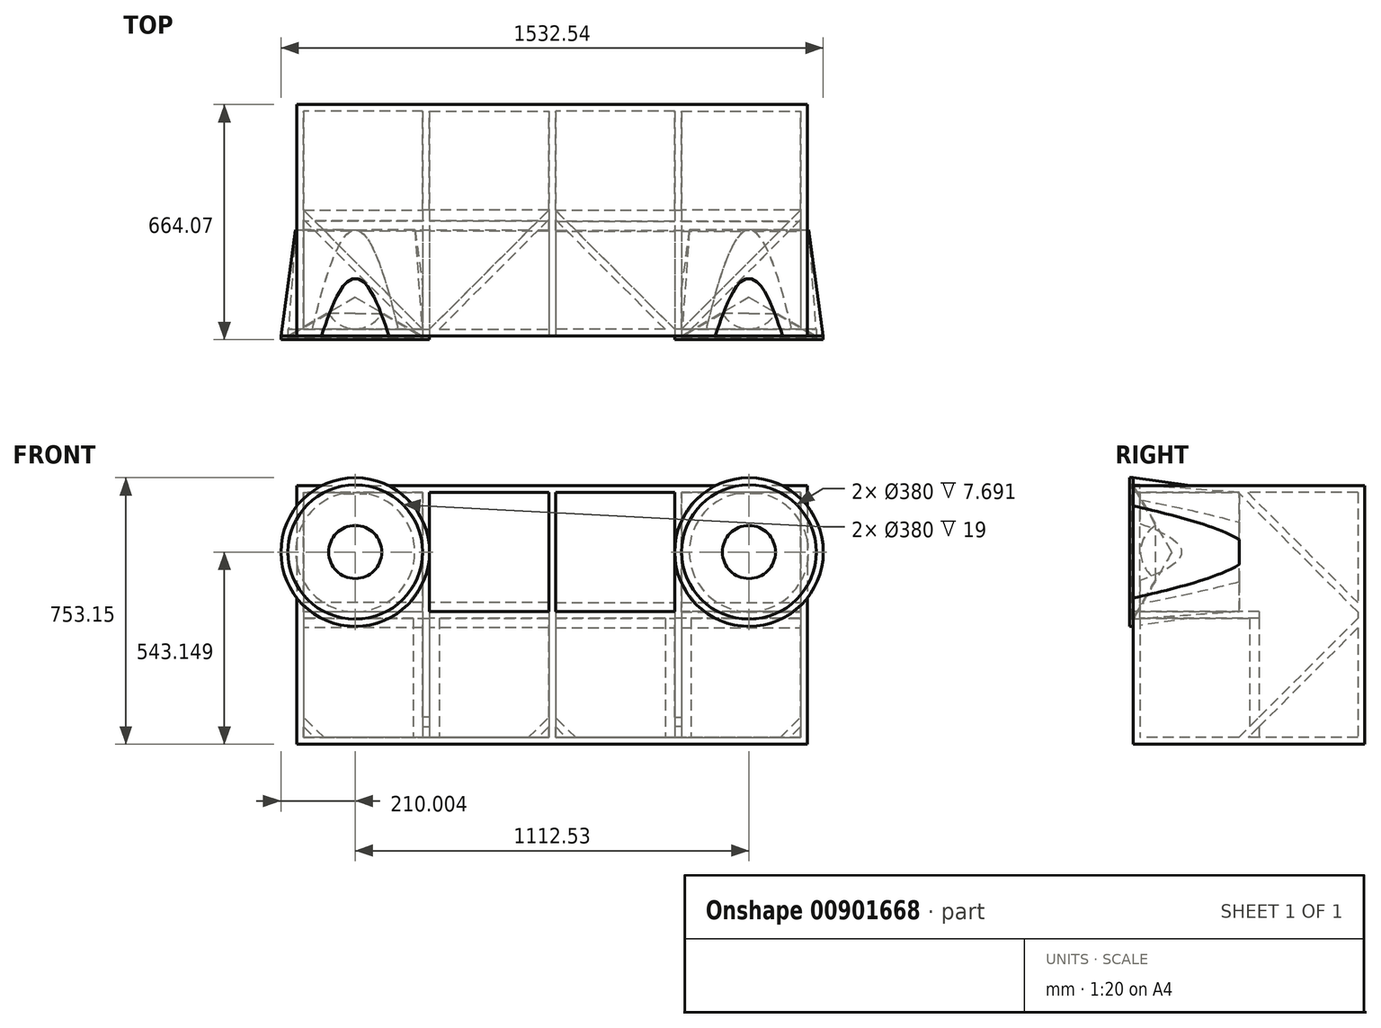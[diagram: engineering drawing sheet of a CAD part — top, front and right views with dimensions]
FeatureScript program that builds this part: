
annotation { "Feature Type Name" : "Feature", "Feature Type Description" : "" }
export const myFeature = defineFeature(function(context is Context, id is Id, definition is map)
    precondition{}
    {
        {
            assignVariable(context, id + "F0", {"variableType" : VariableType.LENGTH, "name" : "Dia", "lengthValue" : 380 * mm});
        }
        {
            assignVariable(context, id + "F1", {"variableType" : VariableType.LENGTH, "name" : "Side", "lengthValue" : sqrt(getVariable(context, 'Dia') * getVariable(context, 'Dia') * PI / 4)});
        }
        {
            assignVariable(context, id + "F2", {"variableType" : VariableType.LENGTH, "name" : "OutsideDia", "lengthValue" : getVariable(context, 'Dia') + 2 * 20 * mm});
        }
        {
            var Q0;
            Q0=qCreatedBy(makeId("Top.planeOp"),FACE);
            var sketch = newSketch(context, id + "F3", { "sketchPlane" : qUnion([Q0])});
            skLineSegment(sketch, "E0.bottom", {"start": v(-721.03, 654.07) * mm, "end": v(9.5, 654.07) * mm});
            skLineSegment(sketch, "E0.top", {"start": v(-721.03, 0) * mm, "end": v(9.5, 0) * mm});
            skLineSegment(sketch, "E0.left", {"start": v(-721.03, 654.07) * mm, "end": v(-721.03, 0) * mm});
            skLineSegment(sketch, "E0.right", {"start": v(9.5, 654.07) * mm, "end": v(9.5, 0) * mm});
            skLineSegment(sketch, "E1.bottom", {"start": v(-702.03, 635.07) * mm, "end": v(-365.27, 635.07) * mm});
            skLineSegment(sketch, "E1.top", {"start": v(-702.03, 19) * mm, "end": v(-392.14, 19) * mm});
            skLineSegment(sketch, "E1.left", {"start": v(-702.03, 635.07) * mm, "end": v(-702.03, 355.77) * mm});
            skLineSegment(sketch, "E1.right", {"start": v(-9.5, 635.07) * mm, "end": v(-9.5, 355.77) * mm});
            skLineSegment(sketch, "E2.top", {"start": v(-365.27, 355.77) * mm, "end": v(-346.27, 355.77) * mm});
            skLineSegment(sketch, "E2.left", {"start": v(-365.27, 635.07) * mm, "end": v(-365.27, 355.77) * mm});
            skLineSegment(sketch, "E2.right", {"start": v(-346.27, 635.07) * mm, "end": v(-346.27, 355.77) * mm});
            skLineSegment(sketch, "E3", {"start": v(-9.5, 355.77) * mm, "end": v(-346.27, 19) * mm});
            skLineSegment(sketch, "E4", {"start": v(-319.4, 19) * mm, "end": v(-9.5, 328.9) * mm});
            skLineSegment(sketch, "E5", {"start": v(-702.03, 355.77) * mm, "end": v(-365.27, 19) * mm});
            skLineSegment(sketch, "E6", {"start": v(-392.14, 19) * mm, "end": v(-702.03, 328.9) * mm});
            skLineSegment(sketch, "E7.trimOffspring", {"start": v(-346.27, 635.07) * mm, "end": v(-9.5, 635.07) * mm});
            skLineSegment(sketch, "E8.trimOffspring", {"start": v(-702.03, 328.9) * mm, "end": v(-702.03, 19) * mm});
            skLineSegment(sketch, "E9.trimOffspring", {"start": v(-365.27, 19) * mm, "end": v(-346.27, 19) * mm});
            skLineSegment(sketch, "E10.trimOffspring", {"start": v(-319.4, 19) * mm, "end": v(-9.5, 19) * mm});
            skLineSegment(sketch, "E11.trimOffspring", {"start": v(-9.5, 328.9) * mm, "end": v(-9.5, 19) * mm});
            skSolve(sketch);
        }
        {
            var Q0;
            Q0 = qSketchRegion(id + "F3", true);
            extrude(context, id + "F4", {"entities" : qUnion([Q0]), "depth" : getVariable(context, 'Side'), "offsetDistance" : 25 * mm});
        }
        {
            var Q0;
            Q0=makeQuery(id+"F4.opExtrude","SWEPT_FACE",FACE,{"disambiguationData":[OSD([sQuery(id+"F3.wireOp",EDGE,"E0.left")])]});
            var sketch = newSketch(context, id + "F5", { "sketchPlane" : qUnion([Q0])});
            skLineSegment(sketch, "E12", {"start": v(-635.07, 336.77) * mm, "end": v(-298.3, 0) * mm});
            skLineSegment(sketch, "E13", {"start": v(-298.3, 0) * mm, "end": v(-325.18, 0) * mm});
            skLineSegment(sketch, "E14", {"start": v(-325.18, 0) * mm, "end": v(-635.07, 309.9) * mm});
            skLineSegment(sketch, "E15", {"start": v(-635.07, 309.9) * mm, "end": v(-635.07, 336.77) * mm});
            skSolve(sketch);
        }
        {
            var Q0;
            Q0 = qSketchRegion(id + "F5", true);
            var Q1;
            Q1=makeQuery(id+"F4.opExtrude","SWEPT_FACE",FACE,{"disambiguationData":[OSD([sQuery(id+"F3.wireOp",EDGE,"E0.right")])]});
            extrude(context, id + "F6", {"entities" : qUnion([Q0]), "operationType" : NewBodyOperationType.ADD, "endBound" : BoundingType.UP_TO_SURFACE, "oppositeDirection" : true, "depth" : 25 * mm, "endBoundEntityFace" : qUnion([Q1]), "offsetDistance" : 25 * mm});
        }
        {
            var Q0;
            Q0=makeQuery(id+"F4.opExtrude","CAP_FACE",FACE,{"disambiguationData":[OSD([sQuery(id+"F3.wireOp",EDGE,"E0.bottom"),sQuery(id+"F3.wireOp",EDGE,"E0.top"),sQuery(id+"F3.wireOp",EDGE,"E0.left"),sQuery(id+"F3.wireOp",EDGE,"E0.right"),sQuery(id+"F3.wireOp",EDGE,"E1.bottom"),sQuery(id+"F3.wireOp",EDGE,"E1.top"),sQuery(id+"F3.wireOp",EDGE,"E1.left"),sQuery(id+"F3.wireOp",EDGE,"E1.right"),sQuery(id+"F3.wireOp",EDGE,"E2.top"),sQuery(id+"F3.wireOp",EDGE,"E2.left"),sQuery(id+"F3.wireOp",EDGE,"E2.right"),sQuery(id+"F3.wireOp",EDGE,"E3"),sQuery(id+"F3.wireOp",EDGE,"E4"),sQuery(id+"F3.wireOp",EDGE,"E5"),sQuery(id+"F3.wireOp",EDGE,"E6"),sQuery(id+"F3.wireOp",EDGE,"E7.trimOffspring"),sQuery(id+"F3.wireOp",EDGE,"E8.trimOffspring"),sQuery(id+"F3.wireOp",EDGE,"E9.trimOffspring"),sQuery(id+"F3.wireOp",EDGE,"E10.trimOffspring"),sQuery(id+"F3.wireOp",EDGE,"E11.trimOffspring")])],"isStart":false});
            var sketch = newSketch(context, id + "F7", { "sketchPlane" : qUnion([Q0])});
            skLineSegment(sketch, "E16.bottom", {"start": v(-721.03, 654.07) * mm, "end": v(9.5, 654.07) * mm});
            skLineSegment(sketch, "E16.top", {"start": v(-721.03, 0) * mm, "end": v(9.5, 0) * mm});
            skLineSegment(sketch, "E16.left", {"start": v(-721.03, 654.07) * mm, "end": v(-721.03, 0) * mm});
            skLineSegment(sketch, "E16.right", {"start": v(9.5, 654.07) * mm, "end": v(9.5, 0) * mm});
            skLineSegment(sketch, "E17.bottom", {"start": v(-702.03, 635.07) * mm, "end": v(-365.27, 635.07) * mm});
            skLineSegment(sketch, "E17.top", {"start": v(-702.03, 355.77) * mm, "end": v(-365.27, 355.77) * mm});
            skLineSegment(sketch, "E17.left", {"start": v(-702.03, 635.07) * mm, "end": v(-702.03, 355.77) * mm});
            skLineSegment(sketch, "E17.right", {"start": v(-365.27, 635.07) * mm, "end": v(-365.27, 355.77) * mm});
            skLineSegment(sketch, "E18.bottom", {"start": v(-9.5, 635.07) * mm, "end": v(-346.27, 635.07) * mm});
            skLineSegment(sketch, "E18.top", {"start": v(-9.5, 355.77) * mm, "end": v(-346.27, 355.77) * mm});
            skLineSegment(sketch, "E18.left", {"start": v(-9.5, 635.07) * mm, "end": v(-9.5, 355.77) * mm});
            skLineSegment(sketch, "E18.right", {"start": v(-346.27, 635.07) * mm, "end": v(-346.27, 355.77) * mm});
            skSolve(sketch);
        }
        {
            var Q0;
            Q0 = qSketchRegion(id + "F7", true);
            extrude(context, id + "F8", {"entities" : qUnion([Q0]), "operationType" : NewBodyOperationType.ADD, "depth" : 19 * mm, "offsetDistance" : 25 * mm});
        }
        {
            var Q0;
            Q0=makeQuery(id+"F8.opExtrude","CAP_FACE",FACE,{"disambiguationData":[OSD([sQuery(id+"F7.wireOp",EDGE,"E16.bottom"),sQuery(id+"F7.wireOp",EDGE,"E16.top"),sQuery(id+"F7.wireOp",EDGE,"E16.left"),sQuery(id+"F7.wireOp",EDGE,"E16.right"),sQuery(id+"F7.wireOp",EDGE,"E17.bottom"),sQuery(id+"F7.wireOp",EDGE,"E17.top"),sQuery(id+"F7.wireOp",EDGE,"E17.left"),sQuery(id+"F7.wireOp",EDGE,"E17.right"),sQuery(id+"F7.wireOp",EDGE,"E18.bottom"),sQuery(id+"F7.wireOp",EDGE,"E18.top"),sQuery(id+"F7.wireOp",EDGE,"E18.left"),sQuery(id+"F7.wireOp",EDGE,"E18.right")])],"isStart":false});
            var sketch = newSketch(context, id + "F9", { "sketchPlane" : qUnion([Q0])});
            skLineSegment(sketch, "E19.bottom", {"start": v(-721.03, 654.07) * mm, "end": v(9.5, 654.07) * mm});
            skLineSegment(sketch, "E19.top", {"start": v(-721.03, 0) * mm, "end": v(9.5, 0) * mm});
            skLineSegment(sketch, "E19.left", {"start": v(-721.03, 654.07) * mm, "end": v(-721.03, 0) * mm});
            skLineSegment(sketch, "E19.right", {"start": v(9.5, 654.07) * mm, "end": v(9.5, 0) * mm});
            skLineSegment(sketch, "E20.bottom", {"start": v(-702.03, 635.07) * mm, "end": v(-365.27, 635.07) * mm});
            skLineSegment(sketch, "E20.top", {"start": v(-702.03, 19) * mm, "end": v(-365.27, 19) * mm});
            skLineSegment(sketch, "E20.left", {"start": v(-702.03, 635.07) * mm, "end": v(-702.03, 19) * mm});
            skLineSegment(sketch, "E20.right", {"start": v(-365.27, 635.07) * mm, "end": v(-365.27, 19) * mm});
            skLineSegment(sketch, "E21.bottom", {"start": v(-9.5, 635.07) * mm, "end": v(-346.27, 635.07) * mm});
            skLineSegment(sketch, "E21.top", {"start": v(-9.5, 19) * mm, "end": v(-346.27, 19) * mm});
            skLineSegment(sketch, "E21.left", {"start": v(-9.5, 635.07) * mm, "end": v(-9.5, 19) * mm});
            skLineSegment(sketch, "E21.right", {"start": v(-346.27, 635.07) * mm, "end": v(-346.27, 19) * mm});
            skSolve(sketch);
        }
        {
            var Q0;
            Q0 = qSketchRegion(id + "F9", true);
            extrude(context, id + "F10", {"entities" : qUnion([Q0]), "operationType" : NewBodyOperationType.ADD, "depth" : getVariable(context, 'Side'), "offsetDistance" : 25 * mm});
        }
        {
            var Q0;
            Q0=makeQuery(id+"F10.boolean.opBoolean","MERGE",FACE,{"derivedFrom":[makeQuery(id+"F8.boolean.opBoolean","MERGE",FACE,{"derivedFrom":[makeQuery(id+"F4.opExtrude","SWEPT_FACE",FACE,{"disambiguationData":[OSD([sQuery(id+"F3.wireOp",EDGE,"E0.left")])]}),makeQuery(id+"F8.opExtrude","SWEPT_FACE",FACE,{"disambiguationData":[OSD([sQuery(id+"F7.wireOp",EDGE,"E16.left")])]})]}),makeQuery(id+"F10.opExtrude","SWEPT_FACE",FACE,{"disambiguationData":[OSD([sQuery(id+"F9.wireOp",EDGE,"E19.left")])]})]});
            var sketch = newSketch(context, id + "F11", { "sketchPlane" : qUnion([Q0])});
            skLineSegment(sketch, "E22", {"start": v(-323.62, 692.53) * mm, "end": v(-296.75, 692.53) * mm});
            skLineSegment(sketch, "E23", {"start": v(-296.75, 692.53) * mm, "end": v(-635.07, 354.21) * mm});
            skLineSegment(sketch, "E24", {"start": v(-635.07, 354.21) * mm, "end": v(-635.07, 381.08) * mm});
            skLineSegment(sketch, "E25", {"start": v(-635.07, 381.08) * mm, "end": v(-323.62, 692.53) * mm});
            skSolve(sketch);
        }
        {
            var Q0;
            Q0 = qSketchRegion(id + "F11", true);
            var Q1;
            Q1=makeQuery(id+"F10.boolean.opBoolean","MERGE",FACE,{"derivedFrom":[makeQuery(id+"F8.boolean.opBoolean","MERGE",FACE,{"derivedFrom":[makeQuery(id+"F4.opExtrude","SWEPT_FACE",FACE,{"disambiguationData":[OSD([sQuery(id+"F3.wireOp",EDGE,"E0.right")])]}),makeQuery(id+"F8.opExtrude","SWEPT_FACE",FACE,{"disambiguationData":[OSD([sQuery(id+"F7.wireOp",EDGE,"E16.right")])]})]}),makeQuery(id+"F10.opExtrude","SWEPT_FACE",FACE,{"disambiguationData":[OSD([sQuery(id+"F9.wireOp",EDGE,"E19.right")])]})]});
            extrude(context, id + "F12", {"entities" : qUnion([Q0]), "operationType" : NewBodyOperationType.ADD, "endBound" : BoundingType.UP_TO_SURFACE, "oppositeDirection" : true, "depth" : 25 * mm, "endBoundEntityFace" : qUnion([Q1]), "offsetDistance" : 25 * mm});
        }
        {
            var Q0;
            Q0=makeQuery(id+"F12.boolean.opBoolean","MERGE",FACE,{"derivedFrom":[makeQuery(id+"F10.opExtrude","CAP_FACE",FACE,{"disambiguationData":[OSD([sQuery(id+"F9.wireOp",EDGE,"E19.bottom"),sQuery(id+"F9.wireOp",EDGE,"E19.top"),sQuery(id+"F9.wireOp",EDGE,"E19.left"),sQuery(id+"F9.wireOp",EDGE,"E19.right"),sQuery(id+"F9.wireOp",EDGE,"E20.bottom"),sQuery(id+"F9.wireOp",EDGE,"E20.top"),sQuery(id+"F9.wireOp",EDGE,"E20.left"),sQuery(id+"F9.wireOp",EDGE,"E20.right"),sQuery(id+"F9.wireOp",EDGE,"E21.bottom"),sQuery(id+"F9.wireOp",EDGE,"E21.top"),sQuery(id+"F9.wireOp",EDGE,"E21.left"),sQuery(id+"F9.wireOp",EDGE,"E21.right")])],"isStart":false}),makeQuery(id+"F12.opExtrude","SWEPT_FACE",FACE,{"disambiguationData":[OSD([sQuery(id+"F11.wireOp",EDGE,"E22")])]})]});
            var sketch = newSketch(context, id + "F13", { "sketchPlane" : qUnion([Q0])});
            skLineSegment(sketch, "E26.bottom", {"start": v(-721.03, 654.07) * mm, "end": v(9.5, 654.07) * mm});
            skLineSegment(sketch, "E26.top", {"start": v(-721.03, 0) * mm, "end": v(9.5, 0) * mm});
            skLineSegment(sketch, "E26.left", {"start": v(-721.03, 654.07) * mm, "end": v(-721.03, 0) * mm});
            skLineSegment(sketch, "E26.right", {"start": v(9.5, 654.07) * mm, "end": v(9.5, 0) * mm});
            skSolve(sketch);
        }
        {
            var Q0;
            Q0 = qSketchRegion(id + "F13", true);
            extrude(context, id + "F14", {"entities" : qUnion([Q0]), "operationType" : NewBodyOperationType.ADD, "depth" : 19 * mm, "offsetDistance" : 25 * mm});
        }
        {
            var Q0;
            Q0=makeQuery(id+"F6.boolean.opBoolean","MERGE",FACE,{"derivedFrom":[makeQuery(id+"F4.opExtrude","CAP_FACE",FACE,{"disambiguationData":[OSD([sQuery(id+"F3.wireOp",EDGE,"E0.bottom"),sQuery(id+"F3.wireOp",EDGE,"E0.top"),sQuery(id+"F3.wireOp",EDGE,"E0.left"),sQuery(id+"F3.wireOp",EDGE,"E0.right"),sQuery(id+"F3.wireOp",EDGE,"E1.bottom"),sQuery(id+"F3.wireOp",EDGE,"E1.top"),sQuery(id+"F3.wireOp",EDGE,"E1.left"),sQuery(id+"F3.wireOp",EDGE,"E1.right"),sQuery(id+"F3.wireOp",EDGE,"E2.top"),sQuery(id+"F3.wireOp",EDGE,"E2.left"),sQuery(id+"F3.wireOp",EDGE,"E2.right"),sQuery(id+"F3.wireOp",EDGE,"E3"),sQuery(id+"F3.wireOp",EDGE,"E4"),sQuery(id+"F3.wireOp",EDGE,"E5"),sQuery(id+"F3.wireOp",EDGE,"E6"),sQuery(id+"F3.wireOp",EDGE,"E7.trimOffspring"),sQuery(id+"F3.wireOp",EDGE,"E8.trimOffspring"),sQuery(id+"F3.wireOp",EDGE,"E9.trimOffspring"),sQuery(id+"F3.wireOp",EDGE,"E10.trimOffspring"),sQuery(id+"F3.wireOp",EDGE,"E11.trimOffspring")])],"isStart":true}),makeQuery(id+"F6.opExtrude","SWEPT_FACE",FACE,{"disambiguationData":[OSD([sQuery(id+"F5.wireOp",EDGE,"E13")])]})]});
            var sketch = newSketch(context, id + "F15", { "sketchPlane" : qUnion([Q0])});
            skLineSegment(sketch, "E27.bottom", {"start": v(-721.03, 0) * mm, "end": v(9.5, 0) * mm});
            skLineSegment(sketch, "E27.top", {"start": v(-721.03, -654.07) * mm, "end": v(9.5, -654.07) * mm});
            skLineSegment(sketch, "E27.left", {"start": v(-721.03, 0) * mm, "end": v(-721.03, -654.07) * mm});
            skLineSegment(sketch, "E27.right", {"start": v(9.5, 0) * mm, "end": v(9.5, -654.07) * mm});
            skSolve(sketch);
        }
        {
            var Q0;
            Q0 = qSketchRegion(id + "F15", true);
            extrude(context, id + "F16", {"entities" : qUnion([Q0]), "operationType" : NewBodyOperationType.ADD, "depth" : 19 * mm, "offsetDistance" : 25 * mm});
        }
        {
            var Q0;
            Q0=makeQuery(id+"F16.boolean.opBoolean","MERGE",FACE,{"derivedFrom":[makeQuery(id+"F14.boolean.opBoolean","MERGE",FACE,{"derivedFrom":[makeQuery(id+"F10.boolean.opBoolean","MERGE",FACE,{"derivedFrom":[makeQuery(id+"F8.boolean.opBoolean","MERGE",FACE,{"derivedFrom":[makeQuery(id+"F4.opExtrude","SWEPT_FACE",FACE,{"disambiguationData":[OSD([sQuery(id+"F3.wireOp",EDGE,"E0.top")])]}),makeQuery(id+"F8.opExtrude","SWEPT_FACE",FACE,{"disambiguationData":[OSD([sQuery(id+"F7.wireOp",EDGE,"E16.top")])]})]}),makeQuery(id+"F10.opExtrude","SWEPT_FACE",FACE,{"disambiguationData":[OSD([sQuery(id+"F9.wireOp",EDGE,"E19.top")])]})]}),makeQuery(id+"F14.opExtrude","SWEPT_FACE",FACE,{"disambiguationData":[OSD([sQuery(id+"F13.wireOp",EDGE,"E26.top")])]})]}),makeQuery(id+"F16.opExtrude","SWEPT_FACE",FACE,{"disambiguationData":[OSD([sQuery(id+"F15.wireOp",EDGE,"E27.bottom")])]})]});
            var sketch = newSketch(context, id + "F17", { "sketchPlane" : qUnion([Q0])});
            skLineSegment(sketch, "E28.bottom", {"start": v(-346.27, 692.53) * mm, "end": v(-9.5, 692.53) * mm});
            skLineSegment(sketch, "E28.top", {"start": v(-346.27, 355.77) * mm, "end": v(-9.5, 355.77) * mm});
            skLineSegment(sketch, "E28.left", {"start": v(-346.27, 692.53) * mm, "end": v(-346.27, 355.77) * mm});
            skLineSegment(sketch, "E28.right", {"start": v(-9.5, 692.53) * mm, "end": v(-9.5, 355.77) * mm});
            skSolve(sketch);
        }
        {
            var Q0;
            Q0 = qSketchRegion(id + "F17", true);
            extrude(context, id + "F18", {"entities" : qUnion([Q0]), "operationType" : NewBodyOperationType.REMOVE, "oppositeDirection" : true, "depth" : 25 * mm, "offsetDistance" : 25 * mm});
        }
        {
            var Q0;
            {var subQ0=sQuery(id+"F9.wireOp",EDGE,"E21.right");var subQ6=sQuery(id+"F7.wireOp",EDGE,"E18.right");var subQ17=sQuery(id+"F3.wireOp",EDGE,"E2.top");var subQ18=makeQuery(id+"F4.opExtrude","SWEPT_FACE",FACE,{"disambiguationData":[OSD([subQ17])]});var subQ28=sQuery(id+"F3.wireOp",EDGE,"E2.right");Q0=makeQuery(id+"F18.boolean.opBoolean","MERGE",FACE,{"derivedFrom":[makeQuery(id+"F12.boolean.opBoolean","SPLIT",FACE,{"disambiguationData":[TD([subQ18])],"derivedFrom":makeQuery(id+"F10.boolean.opBoolean","MERGE",FACE,{"derivedFrom":[makeQuery(id+"F8.boolean.opBoolean","MERGE",FACE,{"derivedFrom":[makeQuery(id+"F6.boolean.opBoolean","SPLIT",FACE,{"disambiguationData":[TD([subQ18])],"derivedFrom":makeQuery(id+"F4.opExtrude","SWEPT_FACE",FACE,{"disambiguationData":[OSD([subQ28])]})}),makeQuery(id+"F8.opExtrude","SWEPT_FACE",FACE,{"disambiguationData":[OSD([subQ6])]})]}),makeQuery(id+"F10.opExtrude","SWEPT_FACE",FACE,{"disambiguationData":[OSD([subQ0])]})]})})],"fromTools":[makeQuery(id+"F18.opExtrude","SWEPT_FACE",FACE,{"disambiguationData":[OSD([sQuery(id+"F17.wireOp",EDGE,"E28.left")])]})]});}
            cPlane(context, id + "F19", {"entities" : qUnion([Q0]), "cplaneType" : CPlaneType.OFFSET, "offset" : getVariable(context, 'OutsideDia') / 2, "oppositeDirection" : true, "width" : 150 * mm, "height" : 150 * mm});
        }
        {
            var Q0;
            Q0=qCreatedBy(id+"F19.planeOp",FACE);
            var sketch = newSketch(context, id + "F20", { "sketchPlane" : qUnion([Q0])});
            skLineSegment(sketch, "E29", {"start": v(0, 524.15) * mm, "end": v(300, 524.15) * mm});
            skLineSegment(sketch, "E30", {"start": v(300, 524.15) * mm, "end": v(300, 355.77) * mm});
            skLineSegment(sketch, "E31", {"start": v(300, 355.77) * mm, "end": v(0, 314.15) * mm});
            skLineSegment(sketch, "E32", {"start": v(0, 314.15) * mm, "end": v(0, 524.15) * mm});
            skPoint(sketch, "E33.0", {"position": v(0, 524.15) * mm});
            skSolve(sketch);
        }
        {
            var Q0;
            Q0 = qSketchRegion(id + "F20", true);
            var Q1;
            Q1=sQuery(id+"F20.wireOp",EDGE,"E29");
            revolve(context, id + "F21", {"operationType" : NewBodyOperationType.ADD, "surfaceOperationType" : NewSurfaceOperationType.NEW, "entities" : qUnion([Q0]), "axis" : qUnion([Q1]), "revolveType" : RevolveType.FULL});
        }
        {
            var Q0;
            Q0=makeQuery(id+"F21.boolean.opBoolean","MERGE",FACE,{"derivedFrom":[makeQuery(id+"F16.boolean.opBoolean","MERGE",FACE,{"derivedFrom":[makeQuery(id+"F14.boolean.opBoolean","MERGE",FACE,{"derivedFrom":[makeQuery(id+"F10.boolean.opBoolean","MERGE",FACE,{"derivedFrom":[makeQuery(id+"F8.boolean.opBoolean","MERGE",FACE,{"derivedFrom":[makeQuery(id+"F4.opExtrude","SWEPT_FACE",FACE,{"disambiguationData":[OSD([sQuery(id+"F3.wireOp",EDGE,"E0.top")])]}),makeQuery(id+"F8.opExtrude","SWEPT_FACE",FACE,{"disambiguationData":[OSD([sQuery(id+"F7.wireOp",EDGE,"E16.top")])]})]}),makeQuery(id+"F10.opExtrude","SWEPT_FACE",FACE,{"disambiguationData":[OSD([sQuery(id+"F9.wireOp",EDGE,"E19.top")])]})]}),makeQuery(id+"F14.opExtrude","SWEPT_FACE",FACE,{"disambiguationData":[OSD([sQuery(id+"F13.wireOp",EDGE,"E26.top")])]})]}),makeQuery(id+"F16.opExtrude","SWEPT_FACE",FACE,{"disambiguationData":[OSD([sQuery(id+"F15.wireOp",EDGE,"E27.bottom")])]})]}),makeQuery(id+"F21.opRevolve","SWEPT_FACE",FACE,{"disambiguationData":[OSD([sQuery(id+"F20.wireOp",EDGE,"E32")])]})]});
            var sketch = newSketch(context, id + "F22", { "sketchPlane" : qUnion([Q0])});
            skCircle(sketch, "E34", {"center": v(-556.27, 524.15) * mm, "radius": 190 * mm});
            skSolve(sketch);
        }
        {
            var Q0;
            Q0 = qSketchRegion(id + "F22", true);
            extrude(context, id + "F23", {"entities" : qUnion([Q0]), "operationType" : NewBodyOperationType.REMOVE, "oppositeDirection" : true, "depth" : 19 * mm, "offsetDistance" : 25 * mm});
        }
        {
            var Q0;
            Q0=qCreatedBy(id+"F19.planeOp",FACE);
            var sketch = newSketch(context, id + "F24", { "sketchPlane" : qUnion([Q0])});
            skLineSegment(sketch, "E35", {"start": v(0, 524.15) * mm, "end": v(300, 524.15) * mm});
            skLineSegment(sketch, "E36", {"start": v(300, 524.15) * mm, "end": v(300, 692.53) * mm});
            skLineSegment(sketch, "E37", {"start": v(300, 692.53) * mm, "end": v(0, 714.15) * mm});
            skLineSegment(sketch, "E38", {"start": v(0, 714.15) * mm, "end": v(0, 524.15) * mm});
            skPoint(sketch, "E39.0", {"position": v(0, 524.15) * mm});
            skSolve(sketch);
        }
        {
            var Q0;
            Q0 = qSketchRegion(id + "F24", true);
            var Q1;
            Q1=sQuery(id+"F24.wireOp",EDGE,"E35");
            revolve(context, id + "F25", {"operationType" : NewBodyOperationType.REMOVE, "surfaceOperationType" : NewSurfaceOperationType.NEW, "entities" : qUnion([Q0]), "axis" : qUnion([Q1]), "revolveType" : RevolveType.FULL, "oppositeDirection" : true});
        }
        {
            var Q0;
            Q0=makeQuery(id+"F4.opExtrude","SWEPT_BODY",BODY,{"disambiguationData":[OSD([sQuery(id+"F3.wireOp",EDGE,"E0.bottom"),sQuery(id+"F3.wireOp",EDGE,"E0.top"),sQuery(id+"F3.wireOp",EDGE,"E0.left"),sQuery(id+"F3.wireOp",EDGE,"E0.right"),sQuery(id+"F3.wireOp",EDGE,"E1.bottom"),sQuery(id+"F3.wireOp",EDGE,"E1.top"),sQuery(id+"F3.wireOp",EDGE,"E1.left"),sQuery(id+"F3.wireOp",EDGE,"E1.right"),sQuery(id+"F3.wireOp",EDGE,"E2.top"),sQuery(id+"F3.wireOp",EDGE,"E2.left"),sQuery(id+"F3.wireOp",EDGE,"E2.right"),sQuery(id+"F3.wireOp",EDGE,"E3"),sQuery(id+"F3.wireOp",EDGE,"E4"),sQuery(id+"F3.wireOp",EDGE,"E5"),sQuery(id+"F3.wireOp",EDGE,"E6"),sQuery(id+"F3.wireOp",EDGE,"E7.trimOffspring"),sQuery(id+"F3.wireOp",EDGE,"E8.trimOffspring"),sQuery(id+"F3.wireOp",EDGE,"E9.trimOffspring"),sQuery(id+"F3.wireOp",EDGE,"E10.trimOffspring"),sQuery(id+"F3.wireOp",EDGE,"E11.trimOffspring")])]});
            var Q1;
            Q1=qCreatedBy(makeId("Right.planeOp"),FACE);
            mirror(context, id + "F26", {"operationType" : NewBodyOperationType.ADD, "entities" : qUnion([Q0]), "mirrorPlane" : qUnion([Q1])});
        }
        {
            var Q0;
            Q0=qCreatedBy(id+"F19.planeOp",FACE);
            var sketch = newSketch(context, id + "F27", { "sketchPlane" : qUnion([Q0])});
            skLineSegment(sketch, "E40", {"start": v(-16.89, 524.15) * mm, "end": v(224.85, 524.15) * mm, "construction": true});
            skLineSegment(sketch, "E41", {"start": v(-10, 734.15) * mm, "end": v(0, 734.15) * mm});
            skLineSegment(sketch, "E42", {"start": v(0, 734.15) * mm, "end": v(0, 714.15) * mm});
            skLineSegment(sketch, "E43", {"start": v(0, 714.15) * mm, "end": v(109.7, 524.15) * mm});
            skLineSegment(sketch, "E44", {"start": v(109.7, 524.15) * mm, "end": v(20.78, 524.15) * mm});
            skLineSegment(sketch, "E45", {"start": v(-2.3, 714.15) * mm, "end": v(64.09, 599.15) * mm});
            skArc(sketch, "E46", {"start": v(64.09, 599.15) * mm, "mid": v(32.39, 567.45) * mm, "end": v(20.78, 524.15) * mm});
            skLineSegment(sketch, "E47", {"start": v(-10, 734.15) * mm, "end": v(-10, 714.15) * mm});
            skLineSegment(sketch, "E48", {"start": v(-10, 714.15) * mm, "end": v(-2.3, 714.15) * mm});
            skLineSegment(sketch, "E49", {"start": v(20.78, 524.15) * mm, "end": v(20.78, 481.17) * mm, "construction": true});
            skLineSegment(sketch, "E50", {"start": v(64.09, 599.15) * mm, "end": v(176.55, 664.08) * mm, "construction": true});
            skSolve(sketch);
        }
        {
            var Q0;
            Q0 = qSketchRegion(id + "F27", true);
            var Q1;
            Q1=sQuery(id+"F27.wireOp",EDGE,"E40");
            revolve(context, id + "F28", {"surfaceOperationType" : NewSurfaceOperationType.NEW, "entities" : qUnion([Q0]), "axis" : qUnion([Q1]), "revolveType" : RevolveType.FULL});
        }
        {
            var Q0;
            Q0=makeQuery(id+"F28.opRevolve","SWEPT_BODY",BODY,{"disambiguationData":[OSD([sQuery(id+"F27.wireOp",EDGE,"E41"),sQuery(id+"F27.wireOp",EDGE,"E42"),sQuery(id+"F27.wireOp",EDGE,"E43"),sQuery(id+"F27.wireOp",EDGE,"E44"),sQuery(id+"F27.wireOp",EDGE,"E45"),sQuery(id+"F27.wireOp",EDGE,"E46"),sQuery(id+"F27.wireOp",EDGE,"E47"),sQuery(id+"F27.wireOp",EDGE,"E48")])]});
            var Q1;
            Q1=qCreatedBy(makeId("Right.planeOp"),FACE);
            mirror(context, id + "F29", {"entities" : qUnion([Q0]), "mirrorPlane" : qUnion([Q1])});
        }
    });
